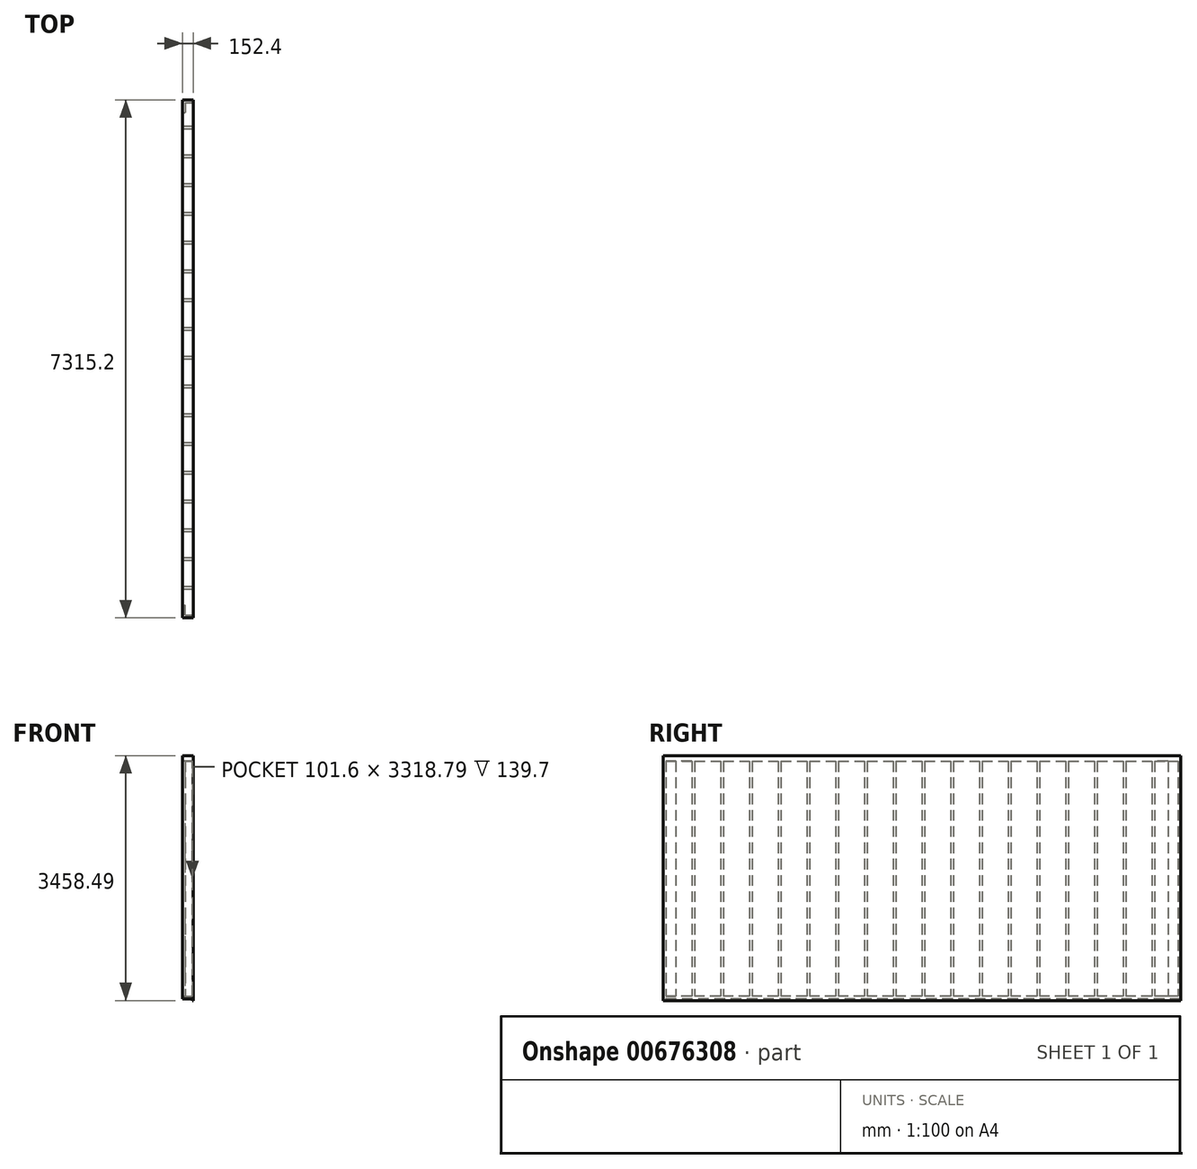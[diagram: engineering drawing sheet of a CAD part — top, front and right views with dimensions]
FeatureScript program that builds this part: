
annotation { "Feature Type Name" : "Feature", "Feature Type Description" : "" }
export const myFeature = defineFeature(function(context is Context, id is Id, definition is map)
    precondition{}
    {
        {
            var Q0;
            Q0=qCreatedBy(makeId("Top.planeOp"),FACE);
            var sketch = newSketch(context, id + "F0", { "sketchPlane" : qUnion([Q0])});
            skLineSegment(sketch, "E0.bottom", {"start": v(-69.85, 3657.6) * mm, "end": v(69.85, 3657.6) * mm});
            skLineSegment(sketch, "E0.top", {"start": v(-69.85, -3657.6) * mm, "end": v(69.85, -3657.6) * mm});
            skLineSegment(sketch, "E0.left", {"start": v(-69.85, 3657.6) * mm, "end": v(-69.85, -3657.6) * mm});
            skLineSegment(sketch, "E0.right", {"start": v(69.85, 3657.6) * mm, "end": v(69.85, -3657.6) * mm});
            skPoint(sketch, "E0.middle", {"position": v(0, 0) * mm});
            skSolve(sketch);
        }
        {
            var Q0;
            Q0=qSketchRegion(id+"F0",true);
            extrude(context, id + "F1", {"entities" : qUnion([Q0]), "depth" : 38.1 * mm, "offsetDistance" : 25.4 * mm});
        }
        {
            var Q0;
            Q0=makeQuery(id+"F1.opExtrude","SWEPT_FACE",FACE,{"disambiguationData":[OSD([sQuery(id+"F0.wireOp",EDGE,"E0.right")])]});
            var sketch = newSketch(context, id + "F2", { "sketchPlane" : qUnion([Q0])});
            skLineSegment(sketch, "E1.bottom", {"start": v(-3657.6, 38.1) * mm, "end": v(3657.6, 38.1) * mm, "construction": true});
            skLineSegment(sketch, "E1.top", {"start": v(-3657.6, 3433.09) * mm, "end": v(3657.6, 3433.09) * mm});
            skLineSegment(sketch, "E1.left", {"start": v(-3657.6, 38.1) * mm, "end": v(-3657.6, 3433.09) * mm});
            skLineSegment(sketch, "E1.right", {"start": v(3657.6, 38.1) * mm, "end": v(3657.6, 3433.09) * mm});
            skLineSegment(sketch, "E2.0", {"start": v(3619.5, 38.1) * mm, "end": v(3619.5, 3356.89) * mm});
            skLineSegment(sketch, "E3.0", {"start": v(-3619.5, 38.1) * mm, "end": v(-3619.5, 3356.89) * mm});
            skLineSegment(sketch, "E4", {"start": v(3619.5, 38.1) * mm, "end": v(3657.6, 38.1) * mm});
            skLineSegment(sketch, "E5.trimOffspring", {"start": v(-3619.5, 3356.89) * mm, "end": v(3619.5, 3356.89) * mm});
            skLineSegment(sketch, "E6", {"start": v(-3657.6, 38.1) * mm, "end": v(-3619.5, 38.1) * mm});
            skSolve(sketch);
        }
        {
            var Q0;
            Q0=qSketchRegion(id+"F2",true);
            var Q1;
            Q1=makeQuery(id+"F1.opExtrude","SWEPT_FACE",FACE,{"disambiguationData":[OSD([sQuery(id+"F0.wireOp",EDGE,"E0.left")])]});
            extrude(context, id + "F3", {"entities" : qUnion([Q0]), "operationType" : NewBodyOperationType.ADD, "endBound" : BoundingType.UP_TO_SURFACE, "oppositeDirection" : true, "depth" : 289.56 * mm, "endBoundEntityFace" : qUnion([Q1]), "offsetDistance" : 25.4 * mm});
        }
        {
            var Q0;
            Q0=makeQuery(id+"F1.opExtrude","CAP_FACE",FACE,{"disambiguationData":[OSD([sQuery(id+"F0.wireOp",EDGE,"E0.bottom"),sQuery(id+"F0.wireOp",EDGE,"E0.top"),sQuery(id+"F0.wireOp",EDGE,"E0.left"),sQuery(id+"F0.wireOp",EDGE,"E0.right")])],"isStart":false});
            var sketch = newSketch(context, id + "F4", { "sketchPlane" : qUnion([Q0])});
            skLineSegment(sketch, "E7.bottom", {"start": v(-69.85, -3619.5) * mm, "end": v(-31.75, -3619.5) * mm});
            skLineSegment(sketch, "E7.top", {"start": v(-69.85, -3479.8) * mm, "end": v(-31.75, -3479.8) * mm});
            skLineSegment(sketch, "E7.left", {"start": v(-69.85, -3619.5) * mm, "end": v(-69.85, -3479.8) * mm});
            skLineSegment(sketch, "E7.right", {"start": v(-31.75, -3619.5) * mm, "end": v(-31.75, -3479.8) * mm});
            skLineSegment(sketch, "E8.bottom", {"start": v(-69.85, -3213.1) * mm, "end": v(69.85, -3213.1) * mm});
            skLineSegment(sketch, "E8.top", {"start": v(-69.85, -3251.2) * mm, "end": v(69.85, -3251.2) * mm});
            skLineSegment(sketch, "E8.left", {"start": v(-69.85, -3213.1) * mm, "end": v(-69.85, -3251.2) * mm});
            skLineSegment(sketch, "E8.right", {"start": v(69.85, -3213.1) * mm, "end": v(69.85, -3251.2) * mm});
            skLineSegment(sketch, "E9.0.1.0", {"start": v(-69.85, -2806.7) * mm, "end": v(69.85, -2806.7) * mm});
            skLineSegment(sketch, "E9.0.1.1", {"start": v(-69.85, -2844.8) * mm, "end": v(69.85, -2844.8) * mm});
            skLineSegment(sketch, "E9.0.1.2", {"start": v(69.85, -2806.7) * mm, "end": v(69.85, -2844.8) * mm});
            skLineSegment(sketch, "E9.0.1.3", {"start": v(-69.85, -2806.7) * mm, "end": v(-69.85, -2844.8) * mm});
            skLineSegment(sketch, "E9.0.2.0", {"start": v(-69.85, -2400.3) * mm, "end": v(69.85, -2400.3) * mm});
            skLineSegment(sketch, "E9.0.2.1", {"start": v(-69.85, -2438.4) * mm, "end": v(69.85, -2438.4) * mm});
            skLineSegment(sketch, "E9.0.2.2", {"start": v(69.85, -2400.3) * mm, "end": v(69.85, -2438.4) * mm});
            skLineSegment(sketch, "E9.0.2.3", {"start": v(-69.85, -2400.3) * mm, "end": v(-69.85, -2438.4) * mm});
            skLineSegment(sketch, "E9.0.3.0", {"start": v(-69.85, -1993.9) * mm, "end": v(69.85, -1993.9) * mm});
            skLineSegment(sketch, "E9.0.3.1", {"start": v(-69.85, -2032) * mm, "end": v(69.85, -2032) * mm});
            skLineSegment(sketch, "E9.0.3.2", {"start": v(69.85, -1993.9) * mm, "end": v(69.85, -2032) * mm});
            skLineSegment(sketch, "E9.0.3.3", {"start": v(-69.85, -1993.9) * mm, "end": v(-69.85, -2032) * mm});
            skLineSegment(sketch, "E9.0.4.0", {"start": v(-69.85, -1587.5) * mm, "end": v(69.85, -1587.5) * mm});
            skLineSegment(sketch, "E9.0.4.1", {"start": v(-69.85, -1625.6) * mm, "end": v(69.85, -1625.6) * mm});
            skLineSegment(sketch, "E9.0.4.2", {"start": v(69.85, -1587.5) * mm, "end": v(69.85, -1625.6) * mm});
            skLineSegment(sketch, "E9.0.4.3", {"start": v(-69.85, -1587.5) * mm, "end": v(-69.85, -1625.6) * mm});
            skLineSegment(sketch, "E9.0.5.0", {"start": v(-69.85, -1181.1) * mm, "end": v(69.85, -1181.1) * mm});
            skLineSegment(sketch, "E9.0.5.1", {"start": v(-69.85, -1219.2) * mm, "end": v(69.85, -1219.2) * mm});
            skLineSegment(sketch, "E9.0.5.2", {"start": v(69.85, -1181.1) * mm, "end": v(69.85, -1219.2) * mm});
            skLineSegment(sketch, "E9.0.5.3", {"start": v(-69.85, -1181.1) * mm, "end": v(-69.85, -1219.2) * mm});
            skLineSegment(sketch, "E9.0.6.0", {"start": v(-69.85, -774.7) * mm, "end": v(69.85, -774.7) * mm});
            skLineSegment(sketch, "E9.0.6.1", {"start": v(-69.85, -812.8) * mm, "end": v(69.85, -812.8) * mm});
            skLineSegment(sketch, "E9.0.6.2", {"start": v(69.85, -774.7) * mm, "end": v(69.85, -812.8) * mm});
            skLineSegment(sketch, "E9.0.6.3", {"start": v(-69.85, -774.7) * mm, "end": v(-69.85, -812.8) * mm});
            skLineSegment(sketch, "E9.0.7.0", {"start": v(-69.85, -368.3) * mm, "end": v(69.85, -368.3) * mm});
            skLineSegment(sketch, "E9.0.7.1", {"start": v(-69.85, -406.4) * mm, "end": v(69.85, -406.4) * mm});
            skLineSegment(sketch, "E9.0.7.2", {"start": v(69.85, -368.3) * mm, "end": v(69.85, -406.4) * mm});
            skLineSegment(sketch, "E9.0.7.3", {"start": v(-69.85, -368.3) * mm, "end": v(-69.85, -406.4) * mm});
            skLineSegment(sketch, "E9.0.8.0", {"start": v(-69.85, 38.1) * mm, "end": v(69.85, 38.1) * mm});
            skLineSegment(sketch, "E9.0.8.1", {"start": v(-69.85, 0) * mm, "end": v(69.85, 0) * mm});
            skLineSegment(sketch, "E9.0.8.2", {"start": v(69.85, 38.1) * mm, "end": v(69.85, 0) * mm});
            skLineSegment(sketch, "E9.0.8.3", {"start": v(-69.85, 38.1) * mm, "end": v(-69.85, 0) * mm});
            skLineSegment(sketch, "E9.0.9.0", {"start": v(-69.85, 444.5) * mm, "end": v(69.85, 444.5) * mm});
            skLineSegment(sketch, "E9.0.9.1", {"start": v(-69.85, 406.4) * mm, "end": v(69.85, 406.4) * mm});
            skLineSegment(sketch, "E9.0.9.2", {"start": v(69.85, 444.5) * mm, "end": v(69.85, 406.4) * mm});
            skLineSegment(sketch, "E9.0.9.3", {"start": v(-69.85, 444.5) * mm, "end": v(-69.85, 406.4) * mm});
            skLineSegment(sketch, "E9.0.10.0", {"start": v(-69.85, 850.9) * mm, "end": v(69.85, 850.9) * mm});
            skLineSegment(sketch, "E9.0.10.1", {"start": v(-69.85, 812.8) * mm, "end": v(69.85, 812.8) * mm});
            skLineSegment(sketch, "E9.0.10.2", {"start": v(69.85, 850.9) * mm, "end": v(69.85, 812.8) * mm});
            skLineSegment(sketch, "E9.0.10.3", {"start": v(-69.85, 850.9) * mm, "end": v(-69.85, 812.8) * mm});
            skLineSegment(sketch, "E9.0.11.0", {"start": v(-69.85, 1257.3) * mm, "end": v(69.85, 1257.3) * mm});
            skLineSegment(sketch, "E9.0.11.1", {"start": v(-69.85, 1219.2) * mm, "end": v(69.85, 1219.2) * mm});
            skLineSegment(sketch, "E9.0.11.2", {"start": v(69.85, 1257.3) * mm, "end": v(69.85, 1219.2) * mm});
            skLineSegment(sketch, "E9.0.11.3", {"start": v(-69.85, 1257.3) * mm, "end": v(-69.85, 1219.2) * mm});
            skLineSegment(sketch, "E9.0.12.0", {"start": v(-69.85, 1663.7) * mm, "end": v(69.85, 1663.7) * mm});
            skLineSegment(sketch, "E9.0.12.1", {"start": v(-69.85, 1625.6) * mm, "end": v(69.85, 1625.6) * mm});
            skLineSegment(sketch, "E9.0.12.2", {"start": v(69.85, 1663.7) * mm, "end": v(69.85, 1625.6) * mm});
            skLineSegment(sketch, "E9.0.12.3", {"start": v(-69.85, 1663.7) * mm, "end": v(-69.85, 1625.6) * mm});
            skLineSegment(sketch, "E9.0.13.0", {"start": v(-69.85, 2070.1) * mm, "end": v(69.85, 2070.1) * mm});
            skLineSegment(sketch, "E9.0.13.1", {"start": v(-69.85, 2032) * mm, "end": v(69.85, 2032) * mm});
            skLineSegment(sketch, "E9.0.13.2", {"start": v(69.85, 2070.1) * mm, "end": v(69.85, 2032) * mm});
            skLineSegment(sketch, "E9.0.13.3", {"start": v(-69.85, 2070.1) * mm, "end": v(-69.85, 2032) * mm});
            skLineSegment(sketch, "E9.0.14.0", {"start": v(-69.85, 2476.5) * mm, "end": v(69.85, 2476.5) * mm});
            skLineSegment(sketch, "E9.0.14.1", {"start": v(-69.85, 2438.4) * mm, "end": v(69.85, 2438.4) * mm});
            skLineSegment(sketch, "E9.0.14.2", {"start": v(69.85, 2476.5) * mm, "end": v(69.85, 2438.4) * mm});
            skLineSegment(sketch, "E9.0.14.3", {"start": v(-69.85, 2476.5) * mm, "end": v(-69.85, 2438.4) * mm});
            skLineSegment(sketch, "E9.0.15.0", {"start": v(-69.85, 2882.9) * mm, "end": v(69.85, 2882.9) * mm});
            skLineSegment(sketch, "E9.0.15.1", {"start": v(-69.85, 2844.8) * mm, "end": v(69.85, 2844.8) * mm});
            skLineSegment(sketch, "E9.0.15.2", {"start": v(69.85, 2882.9) * mm, "end": v(69.85, 2844.8) * mm});
            skLineSegment(sketch, "E9.0.15.3", {"start": v(-69.85, 2882.9) * mm, "end": v(-69.85, 2844.8) * mm});
            skLineSegment(sketch, "E9.0.16.0", {"start": v(-69.85, 3289.3) * mm, "end": v(69.85, 3289.3) * mm});
            skLineSegment(sketch, "E9.0.16.1", {"start": v(-69.85, 3251.2) * mm, "end": v(69.85, 3251.2) * mm});
            skLineSegment(sketch, "E9.0.16.2", {"start": v(69.85, 3289.3) * mm, "end": v(69.85, 3251.2) * mm});
            skLineSegment(sketch, "E9.0.16.3", {"start": v(-69.85, 3289.3) * mm, "end": v(-69.85, 3251.2) * mm});
            skLineSegment(sketch, "E9.direction1", {"start": v(-69.85, -3251.2) * mm, "end": v(-44.45, -3251.2) * mm, "construction": true});
            skLineSegment(sketch, "E9.direction2", {"start": v(-69.85, -3251.2) * mm, "end": v(-69.85, -2844.8) * mm, "construction": true});
            skLineSegment(sketch, "E10.bottom", {"start": v(-69.85, 3619.5) * mm, "end": v(-31.75, 3619.5) * mm});
            skLineSegment(sketch, "E10.top", {"start": v(-69.85, 3479.8) * mm, "end": v(-31.75, 3479.8) * mm});
            skLineSegment(sketch, "E10.left", {"start": v(-69.85, 3619.5) * mm, "end": v(-69.85, 3479.8) * mm});
            skLineSegment(sketch, "E10.right", {"start": v(-31.75, 3619.5) * mm, "end": v(-31.75, 3479.8) * mm});
            skSolve(sketch);
        }
        {
            var Q0;
            Q0 = qSketchRegion(id + "F4", true);
            var Q1;
            Q1=makeQuery(id+"F3.opExtrude","SWEPT_FACE",FACE,{"disambiguationData":[OSD([sQuery(id+"F2.wireOp",EDGE,"E5.trimOffspring")])]});
            extrude(context, id + "F5", {"entities" : qUnion([Q0]), "operationType" : NewBodyOperationType.ADD, "endBound" : BoundingType.UP_TO_SURFACE, "depth" : 25.4 * mm, "endBoundEntityFace" : qUnion([Q1]), "offsetDistance" : 25.4 * mm});
        }
        {
            var Q0;
            Q0=makeQuery(id+"F5.boolean.opBoolean","MERGE",FACE,{"derivedFrom":[makeQuery(id+"F3.boolean.opBoolean","MERGE",FACE,{"derivedFrom":[makeQuery(id+"F1.opExtrude","SWEPT_FACE",FACE,{"disambiguationData":[OSD([sQuery(id+"F0.wireOp",EDGE,"E0.right")])]}),makeQuery(id+"F3.opExtrude","CAP_FACE",FACE,{"disambiguationData":[OSD([sQuery(id+"F2.wireOp",EDGE,"E1.top"),sQuery(id+"F2.wireOp",EDGE,"E1.left"),sQuery(id+"F2.wireOp",EDGE,"E1.right"),sQuery(id+"F2.wireOp",EDGE,"E2.0"),sQuery(id+"F2.wireOp",EDGE,"E3.0"),sQuery(id+"F2.wireOp",EDGE,"E4"),sQuery(id+"F2.wireOp",EDGE,"E5.trimOffspring"),sQuery(id+"F2.wireOp",EDGE,"E6")])],"isStart":true})]}),makeQuery(id+"F5.opExtrude","SWEPT_FACE",FACE,{"disambiguationData":[OSD([sQuery(id+"F4.wireOp",EDGE,"E8.right")])]}),makeQuery(id+"F5.opExtrude","SWEPT_FACE",FACE,{"disambiguationData":[OSD([sQuery(id+"F4.wireOp",EDGE,"E9.0.1.2")])]}),makeQuery(id+"F5.opExtrude","SWEPT_FACE",FACE,{"disambiguationData":[OSD([sQuery(id+"F4.wireOp",EDGE,"E9.0.2.2")])]}),makeQuery(id+"F5.opExtrude","SWEPT_FACE",FACE,{"disambiguationData":[OSD([sQuery(id+"F4.wireOp",EDGE,"E9.0.3.2")])]}),makeQuery(id+"F5.opExtrude","SWEPT_FACE",FACE,{"disambiguationData":[OSD([sQuery(id+"F4.wireOp",EDGE,"E9.0.4.2")])]}),makeQuery(id+"F5.opExtrude","SWEPT_FACE",FACE,{"disambiguationData":[OSD([sQuery(id+"F4.wireOp",EDGE,"E9.0.5.2")])]}),makeQuery(id+"F5.opExtrude","SWEPT_FACE",FACE,{"disambiguationData":[OSD([sQuery(id+"F4.wireOp",EDGE,"E9.0.6.2")])]}),makeQuery(id+"F5.opExtrude","SWEPT_FACE",FACE,{"disambiguationData":[OSD([sQuery(id+"F4.wireOp",EDGE,"E9.0.7.2")])]}),makeQuery(id+"F5.opExtrude","SWEPT_FACE",FACE,{"disambiguationData":[OSD([sQuery(id+"F4.wireOp",EDGE,"E9.0.8.2")])]}),makeQuery(id+"F5.opExtrude","SWEPT_FACE",FACE,{"disambiguationData":[OSD([sQuery(id+"F4.wireOp",EDGE,"E9.0.9.2")])]}),makeQuery(id+"F5.opExtrude","SWEPT_FACE",FACE,{"disambiguationData":[OSD([sQuery(id+"F4.wireOp",EDGE,"E9.0.10.2")])]}),makeQuery(id+"F5.opExtrude","SWEPT_FACE",FACE,{"disambiguationData":[OSD([sQuery(id+"F4.wireOp",EDGE,"E9.0.11.2")])]}),makeQuery(id+"F5.opExtrude","SWEPT_FACE",FACE,{"disambiguationData":[OSD([sQuery(id+"F4.wireOp",EDGE,"E9.0.12.2")])]}),makeQuery(id+"F5.opExtrude","SWEPT_FACE",FACE,{"disambiguationData":[OSD([sQuery(id+"F4.wireOp",EDGE,"E9.0.13.2")])]}),makeQuery(id+"F5.opExtrude","SWEPT_FACE",FACE,{"disambiguationData":[OSD([sQuery(id+"F4.wireOp",EDGE,"E9.0.14.2")])]}),makeQuery(id+"F5.opExtrude","SWEPT_FACE",FACE,{"disambiguationData":[OSD([sQuery(id+"F4.wireOp",EDGE,"E9.0.15.2")])]}),makeQuery(id+"F5.opExtrude","SWEPT_FACE",FACE,{"disambiguationData":[OSD([sQuery(id+"F4.wireOp",EDGE,"E9.0.16.2")])]})]});
            var sketch = newSketch(context, id + "F6", { "sketchPlane" : qUnion([Q0])});
            skLineSegment(sketch, "E11.bottom", {"start": v(-3657.6, 3433.09) * mm, "end": v(3657.6, 3433.09) * mm});
            skLineSegment(sketch, "E11.top", {"start": v(-3657.6, -25.4) * mm, "end": v(3657.6, -25.4) * mm});
            skLineSegment(sketch, "E11.left", {"start": v(-3657.6, 3433.09) * mm, "end": v(-3657.6, -25.4) * mm});
            skLineSegment(sketch, "E11.right", {"start": v(3657.6, 3433.09) * mm, "end": v(3657.6, -25.4) * mm});
            skSolve(sketch);
        }
        {
            var Q0;
            Q0 = qSketchRegion(id + "F6", true);
            extrude(context, id + "F7", {"entities" : qUnion([Q0]), "operationType" : NewBodyOperationType.ADD, "depth" : 12.7 * mm, "offsetDistance" : 25.4 * mm});
        }
    });
